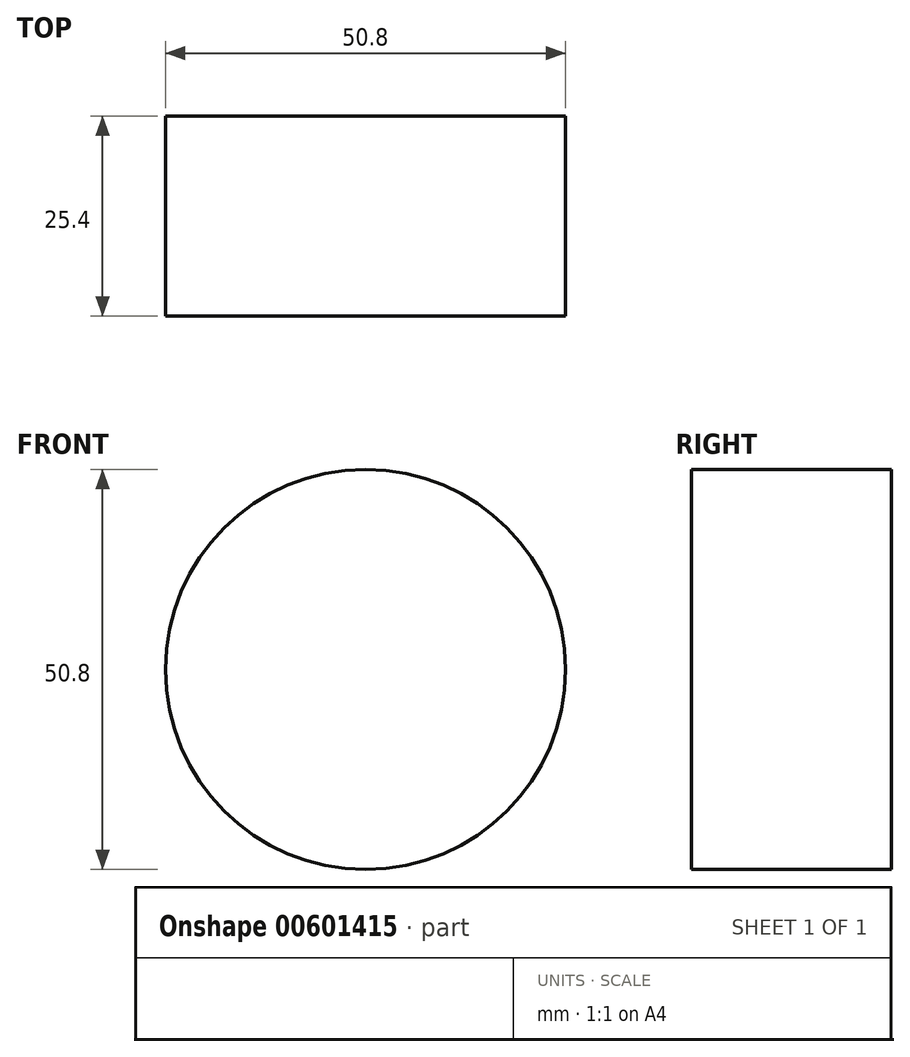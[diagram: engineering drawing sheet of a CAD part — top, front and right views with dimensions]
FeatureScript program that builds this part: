
annotation { "Feature Type Name" : "Feature", "Feature Type Description" : "" }
export const myFeature = defineFeature(function(context is Context, id is Id, definition is map)
    precondition{}
    {
        {
            var Q0;
            Q0=qCreatedBy(makeId("Front.planeOp"),FACE);
            var sketch = newSketch(context, id + "F0", { "sketchPlane" : qUnion([Q0])});
            skCircle(sketch, "E0", {"center": v(0, 0) * mm, "radius": 38.1 * mm});
            skSolve(sketch);
        }
        {
            var Q0;
            Q0=makeQuery(id+"F0.imprint","IMPRINT",FACE,{"disambiguationData":[TD([[makeQuery(id+"F0.imprint","IMPRINT",EDGE,{"derivedFrom":sQuery(id+"F0.wireOp",EDGE,"E0")}),1.0]])]});
            extrude(context, id + "F1", {"entities" : qUnion([Q0]), "depth" : 25.4 * mm, "offsetDistance" : 25.4 * mm});
        }
        {
            var Q0;
            Q0=makeQuery(id+"F1.opExtrude","CAP_FACE",FACE,{"disambiguationData":[OSD([sQuery(id+"F0.wireOp",EDGE,"E0")])],"isStart":false});
            var sketch = newSketch(context, id + "F2", { "sketchPlane" : qUnion([Q0])});
            skCircle(sketch, "E1", {"center": v(0, 0) * mm, "radius": 25.4 * mm});
            skSolve(sketch);
        }
        {
            var Q0;
            Q0=makeQuery(id+"F2.imprint","IMPRINT",FACE,{"disambiguationData":[TD([[makeQuery(id+"F2.imprint","IMPRINT",EDGE,{"derivedFrom":sQuery(id+"F2.wireOp",EDGE,"E1")}),-1.0]])]});
            extrude(context, id + "F3", {"entities" : qUnion([Q0]), "operationType" : NewBodyOperationType.REMOVE, "oppositeDirection" : true, "depth" : 25.4 * mm, "offsetDistance" : 25.4 * mm});
        }
        {
            var Q0;
            Q0=makeQuery(id+"F1.opExtrude","CAP_FACE",FACE,{"disambiguationData":[OSD([sQuery(id+"F0.wireOp",EDGE,"E0")])],"isStart":false});
            var sketch = newSketch(context, id + "F4", { "sketchPlane" : qUnion([Q0])});
            skCircle(sketch, "E2", {"center": v(-30.3, 6.68) * mm, "radius": 3.81 * mm});
            skCircle(sketch, "E3", {"center": v(-22.14, 23.25) * mm, "radius": 3.81 * mm});
            skCircle(sketch, "E4", {"center": v(-6.06, 30.67) * mm, "radius": 3.81 * mm});
            skCircle(sketch, "E5", {"center": v(10.51, 29.43) * mm, "radius": 3.81 * mm});
            skCircle(sketch, "E6", {"center": v(23.12, 22.26) * mm, "radius": 3.81 * mm});
            skCircle(sketch, "E7", {"center": v(30.8, 7.91) * mm, "radius": 3.81 * mm});
            skCircle(sketch, "E8", {"center": v(30.8, -8.16) * mm, "radius": 3.81 * mm});
            skCircle(sketch, "E9", {"center": v(5.07, -30.92) * mm, "radius": 3.81 * mm});
            skCircle(sketch, "E10", {"center": v(-7.8, -30.92) * mm, "radius": 3.81 * mm});
            skCircle(sketch, "E11", {"center": v(-31.53, -8.4) * mm, "radius": 3.81 * mm});
            skCircle(sketch, "E12", {"center": v(22.14, -22.26) * mm, "radius": 3.81 * mm});
            skCircle(sketch, "E13", {"center": v(-22.63, -21.27) * mm, "radius": 3.81 * mm});
            skSolve(sketch);
        }
        {
            var Q0;
            Q0=makeQuery(id+"F4.imprint","IMPRINT",FACE,{"disambiguationData":[TD([[makeQuery(id+"F4.imprint","IMPRINT",EDGE,{"derivedFrom":sQuery(id+"F4.wireOp",EDGE,"E3")}),1.0]])]});
            var Q1;
            Q1=makeQuery(id+"F4.imprint","IMPRINT",FACE,{"disambiguationData":[TD([[makeQuery(id+"F4.imprint","IMPRINT",EDGE,{"derivedFrom":sQuery(id+"F4.wireOp",EDGE,"E4")}),1.0]])]});
            var Q2;
            Q2=makeQuery(id+"F4.imprint","IMPRINT",FACE,{"disambiguationData":[TD([[makeQuery(id+"F4.imprint","IMPRINT",EDGE,{"derivedFrom":sQuery(id+"F4.wireOp",EDGE,"E5")}),1.0]])]});
            var Q3;
            Q3=makeQuery(id+"F4.imprint","IMPRINT",FACE,{"disambiguationData":[TD([[makeQuery(id+"F4.imprint","IMPRINT",EDGE,{"derivedFrom":sQuery(id+"F4.wireOp",EDGE,"E6")}),1.0]])]});
            var Q4;
            Q4=makeQuery(id+"F4.imprint","IMPRINT",FACE,{"disambiguationData":[TD([[makeQuery(id+"F4.imprint","IMPRINT",EDGE,{"derivedFrom":sQuery(id+"F4.wireOp",EDGE,"E7")}),1.0]])]});
            var Q5;
            Q5=makeQuery(id+"F4.imprint","IMPRINT",FACE,{"disambiguationData":[TD([[makeQuery(id+"F4.imprint","IMPRINT",EDGE,{"derivedFrom":sQuery(id+"F4.wireOp",EDGE,"E8")}),1.0]])]});
            var Q6;
            Q6=makeQuery(id+"F4.imprint","IMPRINT",FACE,{"disambiguationData":[TD([[makeQuery(id+"F4.imprint","IMPRINT",EDGE,{"derivedFrom":sQuery(id+"F4.wireOp",EDGE,"E12")}),1.0]])]});
            var Q7;
            Q7=makeQuery(id+"F4.imprint","IMPRINT",FACE,{"disambiguationData":[TD([[makeQuery(id+"F4.imprint","IMPRINT",EDGE,{"derivedFrom":sQuery(id+"F4.wireOp",EDGE,"E9")}),1.0]])]});
            var Q8;
            Q8=makeQuery(id+"F4.imprint","IMPRINT",FACE,{"disambiguationData":[TD([[makeQuery(id+"F4.imprint","IMPRINT",EDGE,{"derivedFrom":sQuery(id+"F4.wireOp",EDGE,"E10")}),1.0]])]});
            var Q9;
            Q9=makeQuery(id+"F4.imprint","IMPRINT",FACE,{"disambiguationData":[TD([[makeQuery(id+"F4.imprint","IMPRINT",EDGE,{"derivedFrom":sQuery(id+"F4.wireOp",EDGE,"E13")}),1.0]])]});
            var Q10;
            Q10=makeQuery(id+"F4.imprint","IMPRINT",FACE,{"disambiguationData":[TD([[makeQuery(id+"F4.imprint","IMPRINT",EDGE,{"derivedFrom":sQuery(id+"F4.wireOp",EDGE,"E11")}),1.0]])]});
            var Q11;
            Q11=makeQuery(id+"F4.imprint","IMPRINT",FACE,{"disambiguationData":[TD([[makeQuery(id+"F4.imprint","IMPRINT",EDGE,{"derivedFrom":sQuery(id+"F4.wireOp",EDGE,"E2")}),1.0]])]});
            extrude(context, id + "F5", {"entities" : qUnion([Q0, Q1, Q2, Q3, Q4, Q5, Q6, Q7, Q8, Q9, Q10, Q11]), "operationType" : NewBodyOperationType.REMOVE, "oppositeDirection" : true, "depth" : 25.4 * mm, "offsetDistance" : 25.4 * mm});
        }
    });
